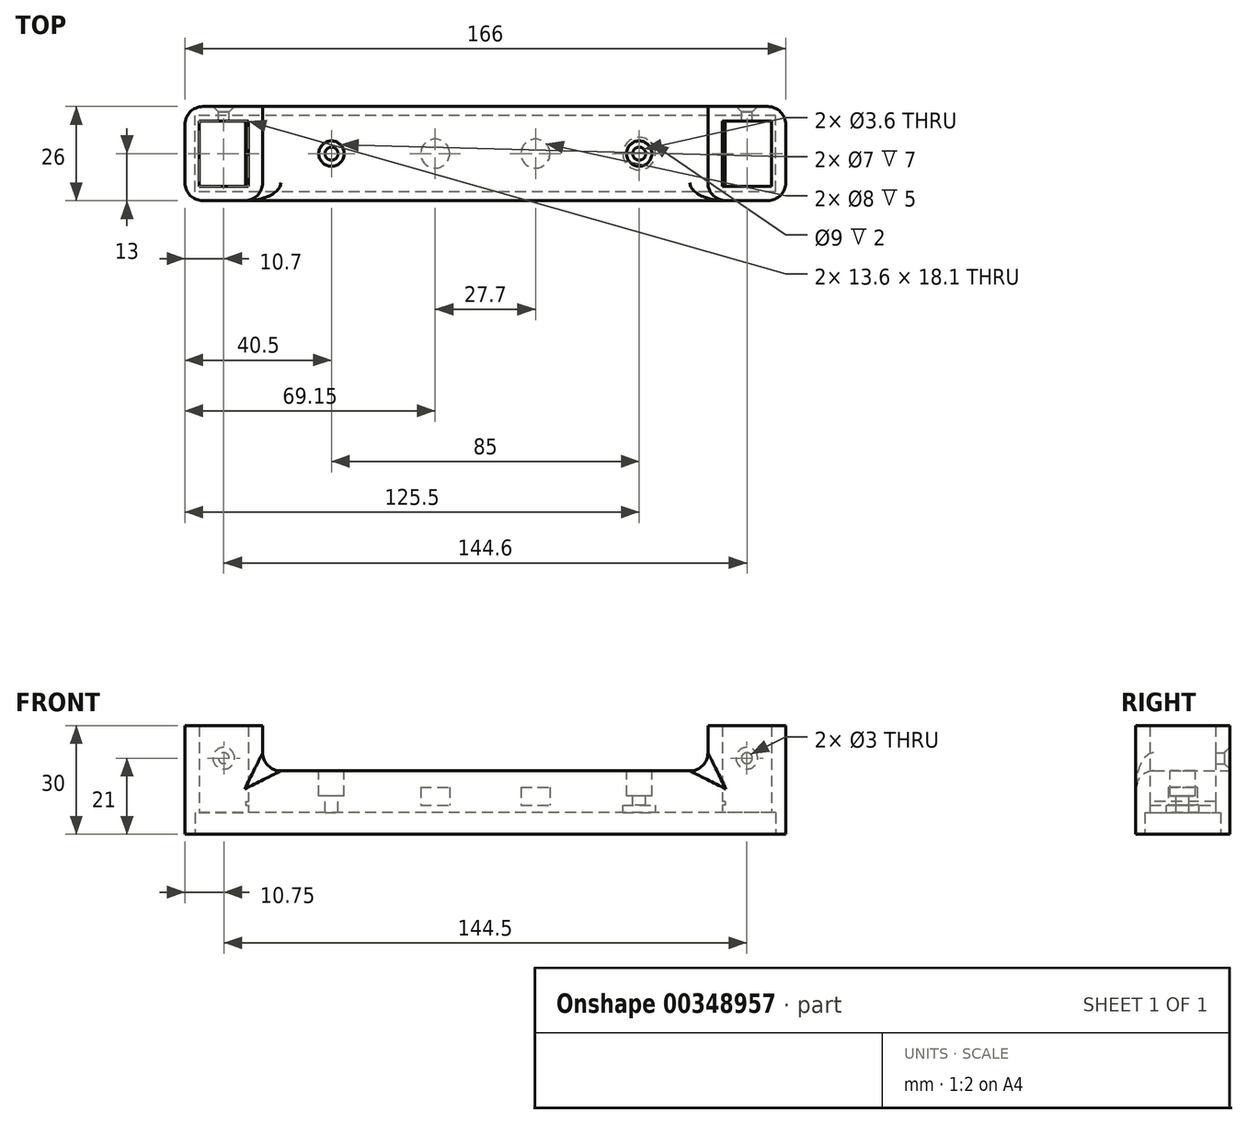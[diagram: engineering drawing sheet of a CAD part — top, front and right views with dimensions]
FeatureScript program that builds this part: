
annotation { "Feature Type Name" : "Feature", "Feature Type Description" : "" }
export const myFeature = defineFeature(function(context is Context, id is Id, definition is map)
    precondition{}
    {
        {
            var Q0;
            Q0=qCreatedBy(makeId("Top.planeOp"),FACE);
            var sketch = newSketch(context, id + "F0", { "sketchPlane" : qUnion([Q0])});
            skLineSegment(sketch, "E0.bottom", {"start": v(83, -13) * mm, "end": v(-83, -13) * mm});
            skLineSegment(sketch, "E0.top", {"start": v(83, 13) * mm, "end": v(-83, 13) * mm});
            skLineSegment(sketch, "E0.left", {"start": v(83, -13) * mm, "end": v(83, 13) * mm});
            skLineSegment(sketch, "E0.right", {"start": v(-83, -13) * mm, "end": v(-83, 13) * mm});
            skPoint(sketch, "E0.middle", {"position": v(0, 0) * mm});
            skLineSegment(sketch, "E1.bottom", {"start": v(80.25, -10.5) * mm, "end": v(-80.25, -10.5) * mm});
            skLineSegment(sketch, "E1.top", {"start": v(80.25, 10.5) * mm, "end": v(-80.25, 10.5) * mm});
            skLineSegment(sketch, "E1.left", {"start": v(80.25, -10.5) * mm, "end": v(80.25, 10.5) * mm});
            skLineSegment(sketch, "E1.right", {"start": v(-80.25, -10.5) * mm, "end": v(-80.25, 10.5) * mm});
            skLineSegment(sketch, "E2.bottom", {"start": v(79.1, -9.05) * mm, "end": v(65.5, -9.05) * mm});
            skLineSegment(sketch, "E2.top", {"start": v(79.1, 9.05) * mm, "end": v(65.5, 9.05) * mm});
            skLineSegment(sketch, "E2.left", {"start": v(79.1, -9.05) * mm, "end": v(79.1, 9.05) * mm});
            skLineSegment(sketch, "E2.right", {"start": v(65.5, -9.05) * mm, "end": v(65.5, 9.05) * mm});
            skPoint(sketch, "E2.middle", {"position": v(72.3, 0) * mm});
            skLineSegment(sketch, "E3.MirrorCS", {"start": v(-65.5, -9.05) * mm, "end": v(-65.5, 9.05) * mm});
            skLineSegment(sketch, "E4.MirrorCS", {"start": v(-79.1, 9.05) * mm, "end": v(-65.5, 9.05) * mm});
            skLineSegment(sketch, "E5.MirrorCS", {"start": v(-79.1, -9.05) * mm, "end": v(-79.1, 9.05) * mm});
            skLineSegment(sketch, "E6.MirrorCS", {"start": v(-79.1, -9.05) * mm, "end": v(-65.5, -9.05) * mm});
            skSolve(sketch);
        }
        {
            var Q0;
            Q0 = qSketchRegion(id + "F0", true);
            var Q1;
            Q1=makeQuery(id+"F0.imprint","IMPRINT",FACE,{"disambiguationData":[TD([[makeQuery(id+"F0.imprint","IMPRINT",EDGE,{"derivedFrom":sQuery(id+"F0.wireOp",EDGE,"E1.bottom")}),-1.0]])]});
            extrude(context, id + "F1", {"entities" : qUnion([Q0, Q1]), "depth" : 30 * mm});
        }
        {
            var Q0;
            Q0=makeQuery(id+"F0.imprint","IMPRINT",FACE,{"disambiguationData":[TD([[makeQuery(id+"F0.imprint","IMPRINT",EDGE,{"derivedFrom":sQuery(id+"F0.wireOp",EDGE,"E1.bottom")}),-1.0]])]});
            extrude(context, id + "F2", {"entities" : qUnion([Q0]), "operationType" : NewBodyOperationType.REMOVE, "depth" : 8 * mm});
        }
        {
            var Q0;
            Q0=makeQuery(id+"F1.opExtrude","SWEPT_FACE",FACE,{"disambiguationData":[OSD([sQuery(id+"F0.wireOp",EDGE,"E0.top")])]});
            var sketch = newSketch(context, id + "F3", { "sketchPlane" : qUnion([Q0])});
            skLineSegment(sketch, "E7.0", {"start": v(-61.5, 30) * mm, "end": v(61.5, 30) * mm});
            skPoint(sketch, "E8.1", {"position": v(65.5, 30) * mm});
            skPoint(sketch, "E9.0", {"position": v(-65.5, 30) * mm});
            skLineSegment(sketch, "E10.top", {"start": v(-61.5, 17.5) * mm, "end": v(61.5, 17.5) * mm});
            skLineSegment(sketch, "E10.left", {"start": v(-61.5, 30) * mm, "end": v(-61.5, 17.5) * mm});
            skLineSegment(sketch, "E10.right", {"start": v(61.5, 30) * mm, "end": v(61.5, 17.5) * mm});
            skSolve(sketch);
        }
        {
            var Q0;
            Q0=makeQuery(id+"F3.imprint","IMPRINT",FACE,{"disambiguationData":[TD([[makeQuery(id+"F3.imprint","IMPRINT",EDGE,{"derivedFrom":sQuery(id+"F3.wireOp",EDGE,"E7.0")}),-1.0]])]});
            extrude(context, id + "F4", {"entities" : qUnion([Q0]), "operationType" : NewBodyOperationType.REMOVE, "endBound" : BoundingType.THROUGH_ALL, "oppositeDirection" : true, "depth" : 25 * mm});
        }
        {
            var Q0;
            Q0=makeQuery(id+"F1.opExtrude","SWEPT_EDGE",EDGE,{"disambiguationData":[OSD([sQuery(id+"F0.wireOp",EDGE,"E0.bottom"),sQuery(id+"F0.wireOp",EDGE,"E0.right")])]});
            var Q1;
            Q1=makeQuery(id+"F1.opExtrude","SWEPT_EDGE",EDGE,{"disambiguationData":[OSD([sQuery(id+"F0.wireOp",EDGE,"E0.bottom"),sQuery(id+"F0.wireOp",EDGE,"E0.left")])]});
            var Q2;
            Q2=makeQuery(id+"F1.opExtrude","SWEPT_EDGE",EDGE,{"disambiguationData":[OSD([sQuery(id+"F0.wireOp",EDGE,"E0.top"),sQuery(id+"F0.wireOp",EDGE,"E0.left")])]});
            var Q3;
            Q3=makeQuery(id+"F1.opExtrude","SWEPT_EDGE",EDGE,{"disambiguationData":[OSD([sQuery(id+"F0.wireOp",EDGE,"E0.top"),sQuery(id+"F0.wireOp",EDGE,"E0.right")])]});
            var Q4;
            Q4=makeQuery(id+"F4.boolean.opBoolean","COPY",EDGE,{"derivedFrom":makeQuery(id+"F4.opExtrude","CAP_EDGE",EDGE,{"disambiguationData":[OSD([sQuery(id+"F3.wireOp",EDGE,"E10.left")])],"isStart":true})});
            var Q5;
            Q5=makeQuery(id+"F4.boolean.opBoolean","COPY",EDGE,{"derivedFrom":makeQuery(id+"F4.opExtrude","CAP_EDGE",EDGE,{"disambiguationData":[OSD([sQuery(id+"F3.wireOp",EDGE,"E10.right")])],"isStart":true})});
            var Q6;
            Q6=makeQuery(id+"F4.boolean.opBoolean","INTERSECT",EDGE,{"derivedFrom":[makeQuery(id+"F1.opExtrude","SWEPT_FACE",FACE,{"disambiguationData":[OSD([sQuery(id+"F0.wireOp",EDGE,"E0.bottom")])]}),makeQuery(id+"F4.opExtrude","SWEPT_FACE",FACE,{"disambiguationData":[OSD([sQuery(id+"F3.wireOp",EDGE,"E10.right")])]})]});
            var Q7;
            Q7=makeQuery(id+"F4.boolean.opBoolean","INTERSECT",EDGE,{"derivedFrom":[makeQuery(id+"F1.opExtrude","SWEPT_FACE",FACE,{"disambiguationData":[OSD([sQuery(id+"F0.wireOp",EDGE,"E0.bottom")])]}),makeQuery(id+"F4.opExtrude","SWEPT_FACE",FACE,{"disambiguationData":[OSD([sQuery(id+"F3.wireOp",EDGE,"E10.left")])]})]});
            fillet(context, id + "F5", {"entities" : qUnion([Q0, Q1, Q2, Q3, Q4, Q5, Q6, Q7]), "radius" : 5 * mm, "tangentPropagation" : true, "allowEdgeOverflow" : false});
        }
        {
            var Q0;
            Q0=makeQuery(id+"F4.boolean.opBoolean","COPY",EDGE,{"derivedFrom":makeQuery(id+"F4.opExtrude","CAP_EDGE",EDGE,{"disambiguationData":[OSD([sQuery(id+"F3.wireOp",EDGE,"E10.top")])],"isStart":true})});
            var Q1;
            Q1=makeQuery(id+"F4.boolean.opBoolean","INTERSECT",EDGE,{"derivedFrom":[makeQuery(id+"F1.opExtrude","SWEPT_FACE",FACE,{"disambiguationData":[OSD([sQuery(id+"F0.wireOp",EDGE,"E0.bottom")])]}),makeQuery(id+"F4.opExtrude","SWEPT_FACE",FACE,{"disambiguationData":[OSD([sQuery(id+"F3.wireOp",EDGE,"E10.top")])]})]});
            fillet(context, id + "F6", {"entities" : qUnion([Q0, Q1]), "radius" : 5 * mm, "tangentPropagation" : true, "allowEdgeOverflow" : false});
        }
        {
            var Q0;
            Q0=makeQuery(id+"F4.boolean.opBoolean","COPY",EDGE,{"derivedFrom":makeQuery(id+"F4.opExtrude","SWEPT_EDGE",EDGE,{"disambiguationData":[OSD([sQuery(id+"F3.wireOp",EDGE,"E10.top"),sQuery(id+"F3.wireOp",EDGE,"E10.left")])]})});
            var Q1;
            Q1=makeQuery(id+"F4.boolean.opBoolean","COPY",EDGE,{"derivedFrom":makeQuery(id+"F4.opExtrude","SWEPT_EDGE",EDGE,{"disambiguationData":[OSD([sQuery(id+"F3.wireOp",EDGE,"E10.top"),sQuery(id+"F3.wireOp",EDGE,"E10.right")])]})});
            fillet(context, id + "F7", {"entities" : qUnion([Q0, Q1]), "radius" : 5 * mm, "tangentPropagation" : true, "allowEdgeOverflow" : false});
        }
        {
            var Q0;
            Q0=makeQuery(id+"F2.boolean.opBoolean","COPY",FACE,{"derivedFrom":makeQuery(id+"F2.opExtrude","CAP_FACE",FACE,{"disambiguationData":[OSD([sQuery(id+"F0.wireOp",EDGE,"E1.bottom"),sQuery(id+"F0.wireOp",EDGE,"E1.top"),sQuery(id+"F0.wireOp",EDGE,"E1.left"),sQuery(id+"F0.wireOp",EDGE,"E1.right"),sQuery(id+"F0.wireOp",EDGE,"E2.bottom"),sQuery(id+"F0.wireOp",EDGE,"E2.top"),sQuery(id+"F0.wireOp",EDGE,"E2.left"),sQuery(id+"F0.wireOp",EDGE,"E2.right"),sQuery(id+"F0.wireOp",EDGE,"E3.MirrorCS"),sQuery(id+"F0.wireOp",EDGE,"E4.MirrorCS"),sQuery(id+"F0.wireOp",EDGE,"E5.MirrorCS"),sQuery(id+"F0.wireOp",EDGE,"E6.MirrorCS")])],"isStart":false})});
            var sketch = newSketch(context, id + "F8", { "sketchPlane" : qUnion([Q0])});
            skPoint(sketch, "E11.0", {"position": v(0, 0) * mm});
            skLineSegment(sketch, "E12", {"start": v(42.5, 0) * mm, "end": v(-42.5, 0) * mm, "construction": true});
            skPoint(sketch, "E13", {"position": v(42.5, 0) * mm});
            skPoint(sketch, "E14", {"position": v(-42.5, 0) * mm});
            skCircle(sketch, "E15", {"center": v(-42.5, 0) * mm, "radius": 4.5 * mm});
            skCircle(sketch, "E16.MirrorC", {"center": v(42.5, 0) * mm, "radius": 4.5 * mm});
            skSolve(sketch);
        }
        {
            var Q0;
            Q0=makeQuery(id+"F8.imprint","IMPRINT",FACE,{"disambiguationData":[TD([[makeQuery(id+"F8.imprint","IMPRINT",EDGE,{"derivedFrom":sQuery(id+"F8.wireOp",EDGE,"E15")}),1.0]])]});
            var Q1;
            Q1=makeQuery(id+"F8.imprint","IMPRINT",FACE,{"disambiguationData":[TD([[makeQuery(id+"F8.imprint","IMPRINT",EDGE,{"derivedFrom":sQuery(id+"F8.wireOp",EDGE,"E16.MirrorC")}),-1.0]])]});
            extrude(context, id + "F9", {"entities" : qUnion([Q0, Q1]), "operationType" : NewBodyOperationType.ADD, "depth" : 2 * mm});
        }
        {
            var Q0;
            Q0=makeQuery(id+"F4.boolean.opBoolean","COPY",FACE,{"derivedFrom":makeQuery(id+"F4.opExtrude","SWEPT_FACE",FACE,{"disambiguationData":[OSD([sQuery(id+"F3.wireOp",EDGE,"E10.top")])]})});
            var sketch = newSketch(context, id + "F10", { "sketchPlane" : qUnion([Q0])});
            skPoint(sketch, "E17.0", {"position": v(-42.5, 0) * mm});
            skPoint(sketch, "E17.1", {"position": v(42.5, 0) * mm});
            skSolve(sketch);
        }
        {
            var Q0;
            Q0=sQuery(id+"F10.wireOp",VERTEX,"E17.0");
            var Q1;
            Q1=sQuery(id+"F10.wireOp",VERTEX,"E17.1");
            var Q2;
            Q2=makeQuery(id+"F1.opExtrude","SWEPT_BODY",BODY,{"disambiguationData":[OSD([sQuery(id+"F0.wireOp",EDGE,"E0.bottom"),sQuery(id+"F0.wireOp",EDGE,"E0.top"),sQuery(id+"F0.wireOp",EDGE,"E0.left"),sQuery(id+"F0.wireOp",EDGE,"E0.right"),sQuery(id+"F0.wireOp",EDGE,"E2.bottom"),sQuery(id+"F0.wireOp",EDGE,"E2.top"),sQuery(id+"F0.wireOp",EDGE,"E2.left"),sQuery(id+"F0.wireOp",EDGE,"E2.right"),sQuery(id+"F0.wireOp",EDGE,"E3.MirrorCS"),sQuery(id+"F0.wireOp",EDGE,"E4.MirrorCS"),sQuery(id+"F0.wireOp",EDGE,"E5.MirrorCS"),sQuery(id+"F0.wireOp",EDGE,"E6.MirrorCS")])]});
            hole(context, id + "F11", {"style" : HoleStyle.C_BORE, "endStyle" : HoleEndStyle.THROUGH, "standardTappedOrClearance" : lookupTablePath({ "standard" : "ISO", "size" : "3.6", "type" : "Drilled" }), "standardBlindInLast" : lookupTablePath({ "standard" : "ISO", "size" : "3.6", "type" : "Drilled" }), "holeDiameter" : 3.6 * mm, "cBoreDiameter" : 7 * mm, "cBoreDepth" : 7 * mm, "isTappedThrough" : true, "tappedDepth" : 6.2 * mm, "tapClearance" : 3, "startFromSketch" : true, "locations" : qUnion([Q0, Q1]), "scope" : qUnion([Q2])});
        }
        {
            var Q0;
            Q0=makeQuery(id+"F1.opExtrude","SWEPT_FACE",FACE,{"disambiguationData":[OSD([sQuery(id+"F0.wireOp",EDGE,"E0.top")])]});
            var sketch = newSketch(context, id + "F12", { "sketchPlane" : qUnion([Q0])});
            skPoint(sketch, "E18", {"position": v(72.25, 21) * mm});
            skPoint(sketch, "E18.positionSnap0", {"position": v(72.25, 30) * mm});
            skPoint(sketch, "E19.MirrorP", {"position": v(-72.25, 21) * mm});
            skSolve(sketch);
        }
        {
            var Q0;
            Q0=sQuery(id+"F12.wireOp",VERTEX,"E18");
            var Q1;
            Q1=sQuery(id+"F12.wireOp",VERTEX,"E19.MirrorP");
            var Q2;
            Q2=makeQuery(id+"F1.opExtrude","SWEPT_BODY",BODY,{"disambiguationData":[OSD([sQuery(id+"F0.wireOp",EDGE,"E0.bottom"),sQuery(id+"F0.wireOp",EDGE,"E0.top"),sQuery(id+"F0.wireOp",EDGE,"E0.left"),sQuery(id+"F0.wireOp",EDGE,"E0.right"),sQuery(id+"F0.wireOp",EDGE,"E2.bottom"),sQuery(id+"F0.wireOp",EDGE,"E2.top"),sQuery(id+"F0.wireOp",EDGE,"E2.left"),sQuery(id+"F0.wireOp",EDGE,"E2.right"),sQuery(id+"F0.wireOp",EDGE,"E3.MirrorCS"),sQuery(id+"F0.wireOp",EDGE,"E4.MirrorCS"),sQuery(id+"F0.wireOp",EDGE,"E5.MirrorCS"),sQuery(id+"F0.wireOp",EDGE,"E6.MirrorCS")])]});
            hole(context, id + "F13", {"style" : HoleStyle.C_SINK, "endStyle" : HoleEndStyle.BLIND, "standardTappedOrClearance" : lookupTablePath({ "standard" : "ISO", "size" : "3", "type" : "Drilled" }), "standardBlindInLast" : lookupTablePath({ "standard" : "ISO", "size" : "3", "type" : "Drilled" }), "holeDiameter" : 3 * mm, "cSinkDiameter" : 6 * mm, "cSinkAngle" : 90 * degree, "holeDepth" : 8 * mm, "isTappedThrough" : true, "tappedDepth" : 6.2 * mm, "tapClearance" : 3, "startFromSketch" : true, "locations" : qUnion([Q0, Q1]), "scope" : qUnion([Q2])});
        }
        {
            var Q0;
            Q0=makeQuery(id+"F2.boolean.opBoolean","COPY",FACE,{"derivedFrom":makeQuery(id+"F2.opExtrude","CAP_FACE",FACE,{"disambiguationData":[OSD([sQuery(id+"F0.wireOp",EDGE,"E1.bottom"),sQuery(id+"F0.wireOp",EDGE,"E1.top"),sQuery(id+"F0.wireOp",EDGE,"E1.left"),sQuery(id+"F0.wireOp",EDGE,"E1.right"),sQuery(id+"F0.wireOp",EDGE,"E2.bottom"),sQuery(id+"F0.wireOp",EDGE,"E2.top"),sQuery(id+"F0.wireOp",EDGE,"E2.left"),sQuery(id+"F0.wireOp",EDGE,"E2.right"),sQuery(id+"F0.wireOp",EDGE,"E3.MirrorCS"),sQuery(id+"F0.wireOp",EDGE,"E4.MirrorCS"),sQuery(id+"F0.wireOp",EDGE,"E5.MirrorCS"),sQuery(id+"F0.wireOp",EDGE,"E6.MirrorCS")])],"isStart":false})});
            var sketch = newSketch(context, id + "F14", { "sketchPlane" : qUnion([Q0])});
            skPoint(sketch, "E20.0", {"position": v(0, 0) * mm});
            skLineSegment(sketch, "E21", {"start": v(13.85, 0) * mm, "end": v(-13.85, 0) * mm, "construction": true});
            skCircle(sketch, "E22", {"center": v(-13.85, 0) * mm, "radius": 4 * mm});
            skCircle(sketch, "E23.MirrorC", {"center": v(13.85, 0) * mm, "radius": 4 * mm});
            skSolve(sketch);
        }
        {
            var Q0;
            Q0 = qSketchRegion(id + "F14", true);
            extrude(context, id + "F15", {"entities" : qUnion([Q0]), "operationType" : NewBodyOperationType.REMOVE, "oppositeDirection" : true, "depth" : 5 * mm});
        }
        {
            var Q0;
            Q0=makeQuery(id+"F1.opExtrude","SWEPT_FACE",FACE,{"disambiguationData":[OSD([sQuery(id+"F0.wireOp",EDGE,"E2.right")])]});
            var sketch = newSketch(context, id + "F16", { "sketchPlane" : qUnion([Q0])});
            skLineSegment(sketch, "E24.0", {"start": v(-9.05, 8) * mm, "end": v(9.05, 8) * mm});
            skLineSegment(sketch, "E25.bottom", {"start": v(9.05, 8) * mm, "end": v(-9.05, 8) * mm});
            skLineSegment(sketch, "E25.top", {"start": v(9.05, 9) * mm, "end": v(-9.05, 9) * mm});
            skLineSegment(sketch, "E25.left", {"start": v(9.05, 8) * mm, "end": v(9.05, 9) * mm});
            skLineSegment(sketch, "E25.right", {"start": v(-9.05, 8) * mm, "end": v(-9.05, 9) * mm});
            skSolve(sketch);
        }
        {
            var Q0;
            Q0 = qSketchRegion(id + "F16", true);
            extrude(context, id + "F17", {"entities" : qUnion([Q0]), "operationType" : NewBodyOperationType.ADD, "depth" : .75 * mm});
        }
        {
            var Q0;
            Q0=makeQuery(id+"F1.opExtrude","SWEPT_FACE",FACE,{"disambiguationData":[OSD([sQuery(id+"F0.wireOp",EDGE,"E3.MirrorCS")])]});
            var sketch = newSketch(context, id + "F18", { "sketchPlane" : qUnion([Q0])});
            skLineSegment(sketch, "E26.bottom", {"start": v(9.05, 8) * mm, "end": v(-9.05, 8) * mm});
            skLineSegment(sketch, "E26.top", {"start": v(9.05, 9) * mm, "end": v(-9.05, 9) * mm});
            skLineSegment(sketch, "E26.left", {"start": v(9.05, 8) * mm, "end": v(9.05, 9) * mm});
            skLineSegment(sketch, "E26.right", {"start": v(-9.05, 8) * mm, "end": v(-9.05, 9) * mm});
            skSolve(sketch);
        }
        {
            var Q0;
            Q0 = qSketchRegion(id + "F18", true);
            extrude(context, id + "F19", {"entities" : qUnion([Q0]), "operationType" : NewBodyOperationType.ADD, "depth" : .75 * mm});
        }
    });
